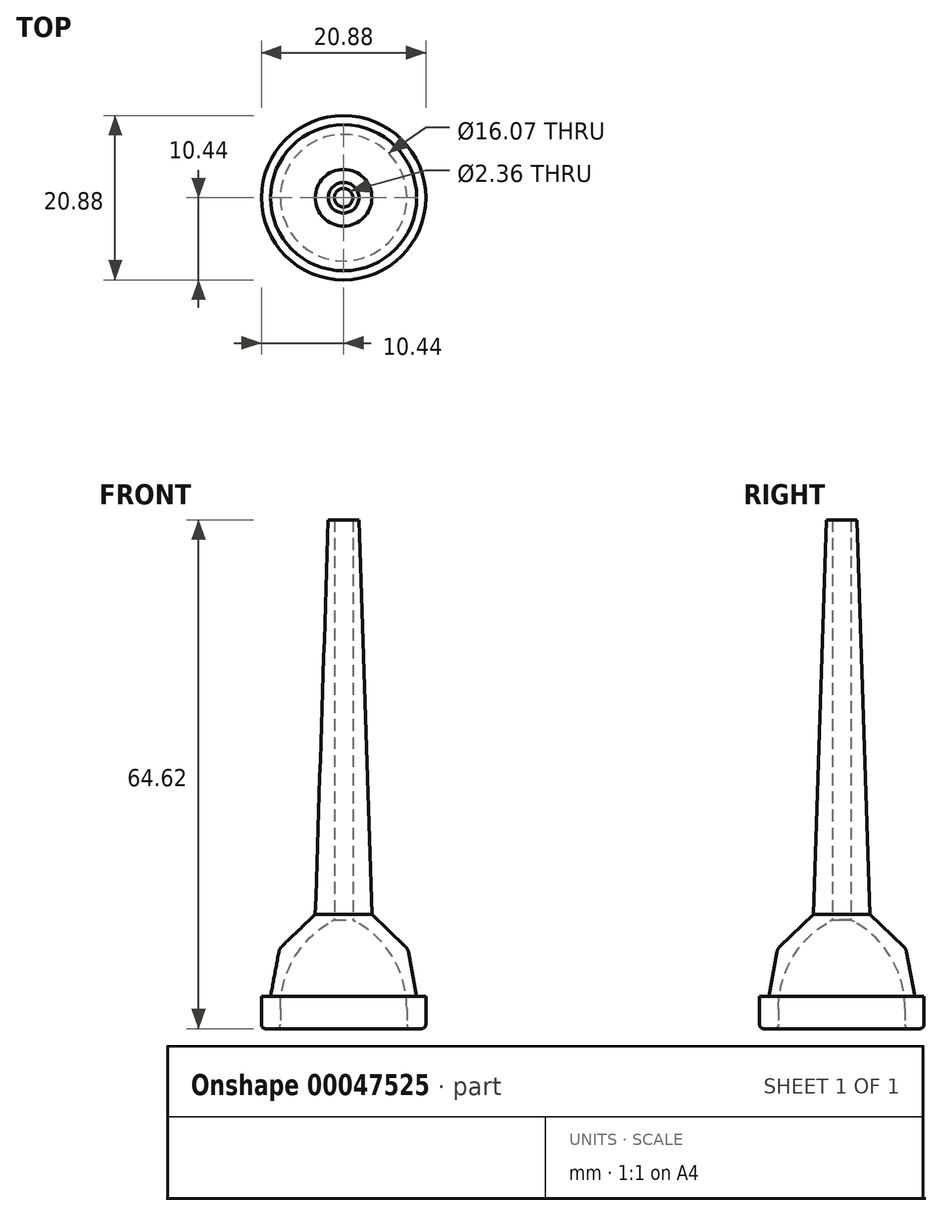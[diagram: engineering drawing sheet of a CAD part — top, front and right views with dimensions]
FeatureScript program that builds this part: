
annotation { "Feature Type Name" : "Feature", "Feature Type Description" : "" }
export const myFeature = defineFeature(function(context is Context, id is Id, definition is map)
    precondition{}
    {
        {
            var Q0;
            Q0=qCreatedBy(makeId("Front.planeOp"),FACE);
            var sketch = newSketch(context, id + "F0", { "sketchPlane" : qUnion([Q0])});
            skLineSegment(sketch, "E0", {"start": v(-8.04, 0) * mm, "end": v(8.04, 0) * mm});
            skLineSegment(sketch, "E1", {"start": v(-8.04, 0.53) * mm, "end": v(-8.04, 2.54) * mm});
            skLineSegment(sketch, "E2", {"start": v(8.04, 2.54) * mm, "end": v(8.04, 0) * mm});
            skPoint(sketch, "E3.visualSharp", {"position": v(-8.04, 7.8) * mm});
            skArc(sketch, "E3.filletArc", {"start": v(-1.53, 13.63) * mm, "mid": v(-6.29, 8.97) * mm, "end": v(-8.04, 2.54) * mm});
            skPoint(sketch, "E4.visualSharp", {"position": v(8.04, 7.8) * mm});
            skArc(sketch, "E4.filletArc", {"start": v(8.04, 2.54) * mm, "mid": v(7.07, 7.4) * mm, "end": v(4.32, 11.52) * mm});
            skLineSegment(sketch, "E5", {"start": v(-1.53, 13.63) * mm, "end": v(-1.18, 13.82) * mm});
            skLineSegment(sketch, "E6", {"start": v(4.32, 11.52) * mm, "end": v(1.9, 13.93) * mm});
            skLineSegment(sketch, "E7", {"start": v(-10.44, 0.53) * mm, "end": v(-10.44, 4.1) * mm});
            skLineSegment(sketch, "E8", {"start": v(-10.44, 4.1) * mm, "end": v(-9.28, 4.1) * mm});
            skLineSegment(sketch, "E9", {"start": v(-8.04, 0) * mm, "end": v(-10.44, 0) * mm});
            skLineSegment(sketch, "E10", {"start": v(-9.9, 0) * mm, "end": v(-8.57, 0) * mm});
            skLineSegment(sketch, "E11", {"start": v(-1.18, 13.82) * mm, "end": v(-1.18, 64.62) * mm});
            skLineSegment(sketch, "E12", {"start": v(-1.18, 64.62) * mm, "end": v(-1.94, 64.62) * mm});
            skLineSegment(sketch, "E13", {"start": v(-3.6, 14.75) * mm, "end": v(-3.7, 14.64) * mm});
            skLineSegment(sketch, "E14", {"start": v(-3.7, 14.64) * mm, "end": v(-3.6, 14.54) * mm});
            skLineSegment(sketch, "E15", {"start": v(-3.6, 14.54) * mm, "end": v(-7.83, 10.47) * mm});
            skLineSegment(sketch, "E16", {"start": v(-8.23, 9.73) * mm, "end": v(-9.28, 4.1) * mm});
            skPoint(sketch, "E17.visualSharp", {"position": v(-8.15, 10.16) * mm});
            skArc(sketch, "E17.filletArc", {"start": v(-7.83, 10.47) * mm, "mid": v(-8.09, 10.13) * mm, "end": v(-8.23, 9.73) * mm});
            skLineSegment(sketch, "E18", {"start": v(0, 0) * mm, "end": v(0, 70.32) * mm});
            skLineSegment(sketch, "E19", {"start": v(-1.94, 64.62) * mm, "end": v(-3.6, 14.54) * mm});
            skPoint(sketch, "E20.visualSharp", {"position": v(-8.04, 0) * mm});
            skArc(sketch, "E20.filletArc", {"start": v(-8.57, 0) * mm, "mid": v(-8.2, 0.16) * mm, "end": v(-8.04, 0.53) * mm});
            skPoint(sketch, "E21.visualSharp", {"position": v(-10.44, 0) * mm});
            skArc(sketch, "E21.filletArc", {"start": v(-10.44, 0.53) * mm, "mid": v(-10.28, 0.16) * mm, "end": v(-9.9, 0) * mm});
            skSolve(sketch);
        }
        {
            var Q0;
            Q0=makeQuery(id+"F0.imprint","IMPRINT",FACE,{"disambiguationData":[TD([[makeQuery(id+"F0.imprint","IMPRINT",EDGE,{"derivedFrom":sQuery(id+"F0.wireOp",EDGE,"E1")}),1.0]])]});
            var Q1;
            Q1=sQuery(id+"F0.wireOp",EDGE,"E18");
            revolve(context, id + "F1", {"entities" : qUnion([Q0]), "axis" : qUnion([Q1]), "revolveType" : RevolveType.FULL});
        }
    });
